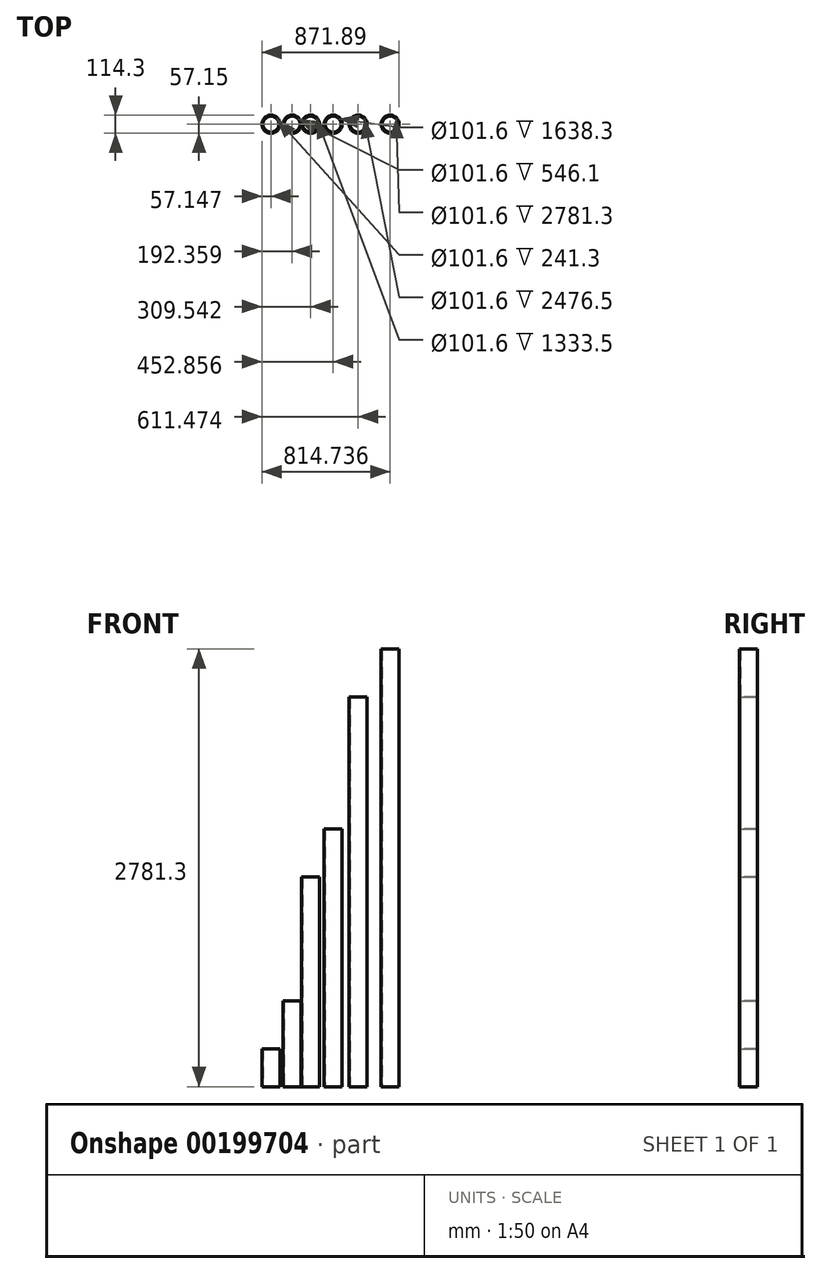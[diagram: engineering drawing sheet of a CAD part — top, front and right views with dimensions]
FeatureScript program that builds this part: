
annotation { "Feature Type Name" : "Feature", "Feature Type Description" : "" }
export const myFeature = defineFeature(function(context is Context, id is Id, definition is map)
    precondition{}
    {
        {
            var Q0;
            Q0=qCreatedBy(makeId("Top.planeOp"),FACE);
            var sketch = newSketch(context, id + "F0", { "sketchPlane" : qUnion([Q0])});
            skCircle(sketch, "E0", {"center": v(-315.24, 0) * mm, "radius": 57.15 * mm});
            skCircle(sketch, "E1", {"center": v(-180.03, 0) * mm, "radius": 57.15 * mm});
            skCircle(sketch, "E2", {"center": v(-62.85, 0) * mm, "radius": 57.15 * mm});
            skCircle(sketch, "E3", {"center": v(80.47, 0) * mm, "radius": 57.15 * mm});
            skCircle(sketch, "E4", {"center": v(239.08, 0) * mm, "radius": 57.15 * mm});
            skCircle(sketch, "E5", {"center": v(442.35, 0) * mm, "radius": 57.15 * mm});
            skCircle(sketch, "E6", {"center": v(-315.24, 0) * mm, "radius": 50.8 * mm});
            skCircle(sketch, "E7", {"center": v(-180.03, 0) * mm, "radius": 50.8 * mm});
            skCircle(sketch, "E8", {"center": v(-62.85, 0) * mm, "radius": 50.8 * mm});
            skCircle(sketch, "E9", {"center": v(80.47, 0) * mm, "radius": 50.8 * mm});
            skCircle(sketch, "E10", {"center": v(239.08, 0) * mm, "radius": 50.8 * mm});
            skCircle(sketch, "E11", {"center": v(442.35, 0) * mm, "radius": 50.8 * mm});
            skSolve(sketch);
        }
        {
            var Q0;
            Q0 = qSketchRegion(id + "F0", true);
            extrude(context, id + "F1", {"entities" : qUnion([Q0]), "depth" : 241.3 * mm});
        }
        {
            var Q0;
            Q0=makeQuery(id+"F1.opExtrude","CAP_FACE",FACE,{"disambiguationData":[OSD([sQuery(id+"F0.wireOp",EDGE,"E1"),sQuery(id+"F0.wireOp",EDGE,"E7")])],"isStart":false});
            extrude(context, id + "F2", {"entities" : qUnion([Q0]), "operationType" : NewBodyOperationType.ADD, "depth" : 304.8 * mm});
        }
        {
            var Q0;
            Q0=makeQuery(id+"F1.opExtrude","CAP_FACE",FACE,{"disambiguationData":[OSD([sQuery(id+"F0.wireOp",EDGE,"E2"),sQuery(id+"F0.wireOp",EDGE,"E8")])],"isStart":false});
            extrude(context, id + "F3", {"entities" : qUnion([Q0]), "operationType" : NewBodyOperationType.ADD, "depth" : 1092.2 * mm});
        }
        {
            var Q0;
            Q0=makeQuery(id+"F1.opExtrude","CAP_FACE",FACE,{"disambiguationData":[OSD([sQuery(id+"F0.wireOp",EDGE,"E3"),sQuery(id+"F0.wireOp",EDGE,"E9")])],"isStart":false});
            extrude(context, id + "F4", {"entities" : qUnion([Q0]), "operationType" : NewBodyOperationType.ADD, "depth" : 1397 * mm});
        }
        {
            var Q0;
            Q0=makeQuery(id+"F1.opExtrude","CAP_FACE",FACE,{"disambiguationData":[OSD([sQuery(id+"F0.wireOp",EDGE,"E4"),sQuery(id+"F0.wireOp",EDGE,"E10")])],"isStart":false});
            extrude(context, id + "F5", {"entities" : qUnion([Q0]), "operationType" : NewBodyOperationType.ADD, "depth" : 2235.2 * mm});
        }
        {
            var Q0;
            Q0=makeQuery(id+"F1.opExtrude","CAP_FACE",FACE,{"disambiguationData":[OSD([sQuery(id+"F0.wireOp",EDGE,"E5"),sQuery(id+"F0.wireOp",EDGE,"E11")])],"isStart":false});
            extrude(context, id + "F6", {"entities" : qUnion([Q0]), "operationType" : NewBodyOperationType.ADD, "depth" : 2540 * mm});
        }
    });
